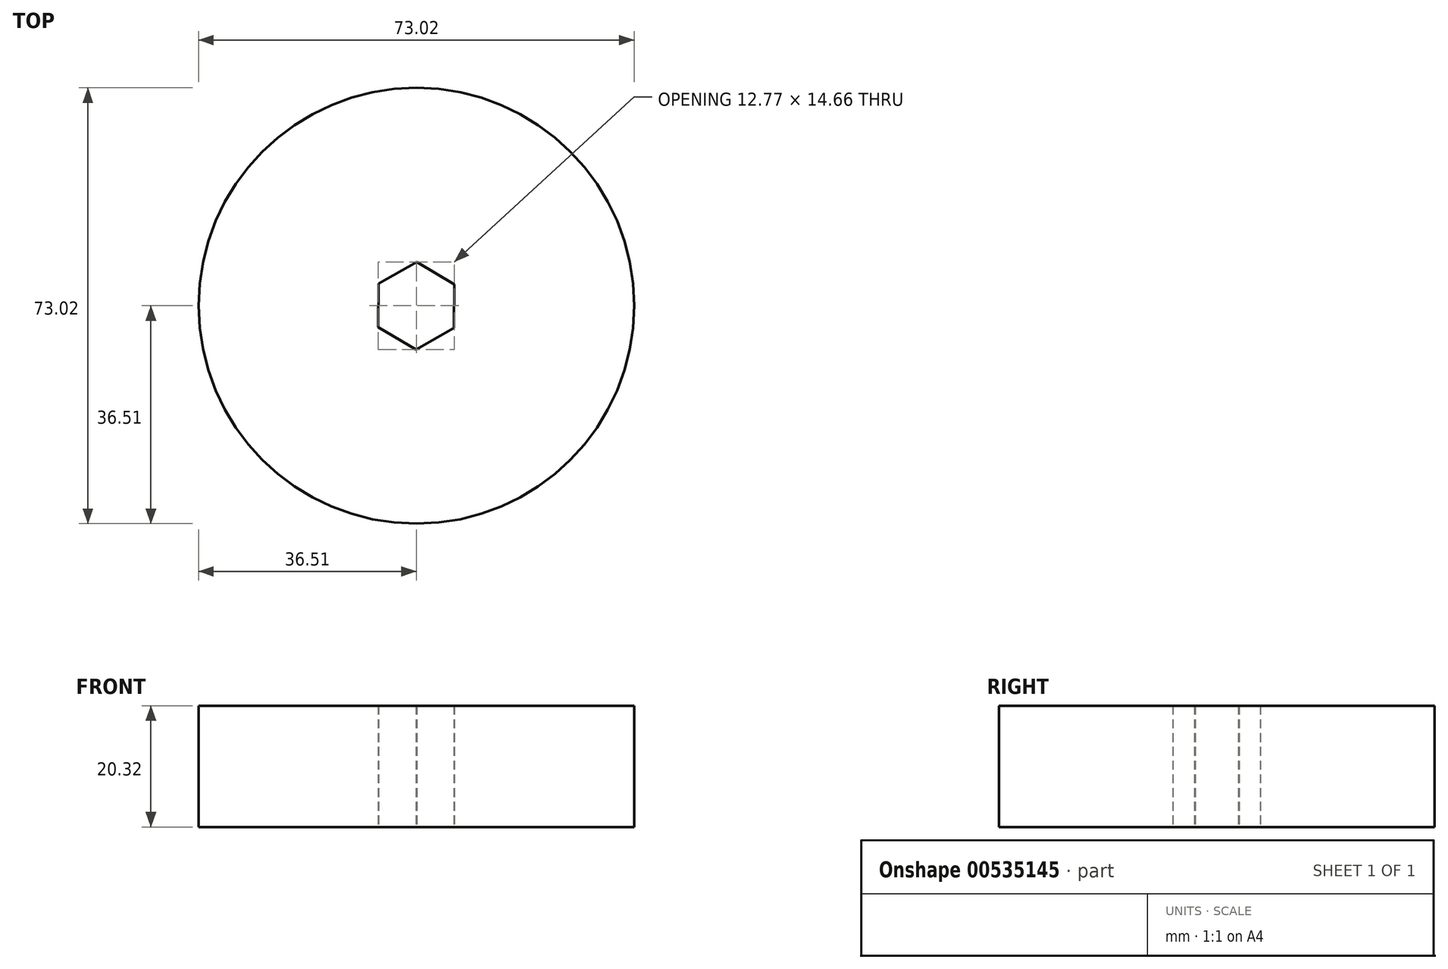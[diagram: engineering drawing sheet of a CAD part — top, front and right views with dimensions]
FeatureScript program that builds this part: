
annotation { "Feature Type Name" : "Feature", "Feature Type Description" : "" }
export const myFeature = defineFeature(function(context is Context, id is Id, definition is map)
    precondition{}
    {
        {
            var Q0;
            Q0=qCreatedBy(makeId("Top.planeOp"),FACE);
            var sketch = newSketch(context, id + "F0", { "sketchPlane" : qUnion([Q0])});
            skCircle(sketch, "E0", {"center": v(0, 0) * mm, "radius": 36.51 * mm});
            skCircle(sketch, "E1.cCircle", {"center": v(0, 0) * mm, "radius": 6.35 * mm, "construction": true});
            skLineSegment(sketch, "E1.0", {"start": v(-6.32, 3.73) * mm, "end": v(0.07, 7.33) * mm});
            skLineSegment(sketch, "E1.1", {"start": v(0.07, 7.33) * mm, "end": v(6.38, 3.6) * mm});
            skLineSegment(sketch, "E1.2", {"start": v(6.38, 3.6) * mm, "end": v(6.32, -3.73) * mm});
            skLineSegment(sketch, "E1.3", {"start": v(6.32, -3.73) * mm, "end": v(-0.07, -7.33) * mm});
            skLineSegment(sketch, "E1.4", {"start": v(-0.07, -7.33) * mm, "end": v(-6.38, -3.6) * mm});
            skLineSegment(sketch, "E1.5", {"start": v(-6.38, -3.6) * mm, "end": v(-6.32, 3.73) * mm});
            skPoint(sketch, "E1.0.midPoint", {"position": v(-3.12, 5.53) * mm});
            skSolve(sketch);
        }
        {
            var Q0;
            Q0=qSketchRegion(id+"F0",true);
            extrude(context, id + "F1", {"entities" : qUnion([Q0]), "depth" : 20.32 * mm});
        }
    });
